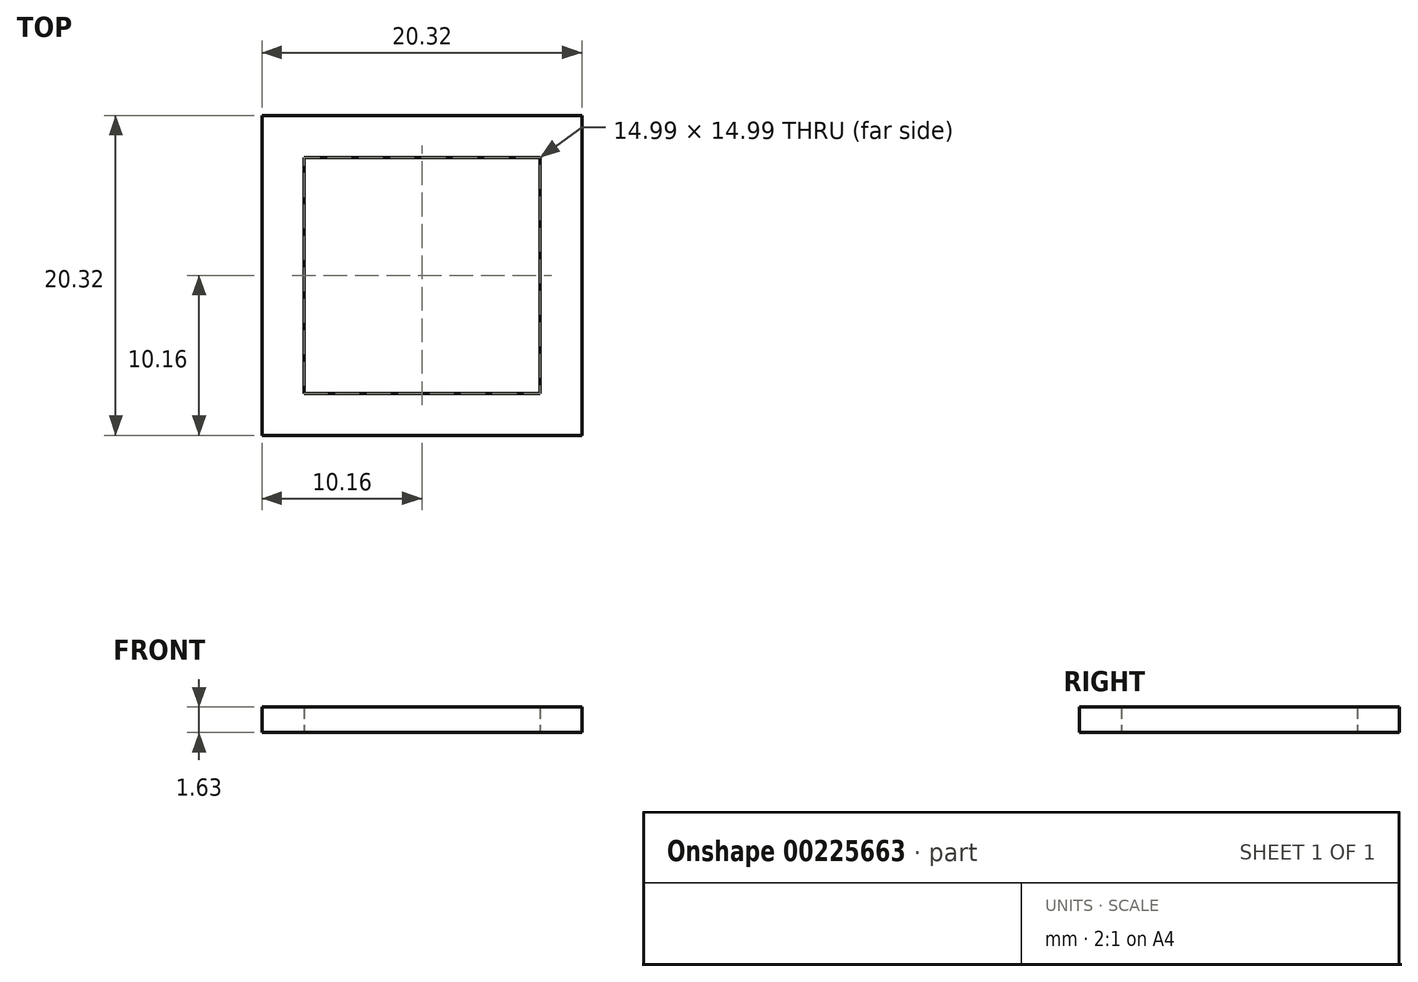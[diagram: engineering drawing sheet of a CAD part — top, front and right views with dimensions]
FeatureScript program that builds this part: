
annotation { "Feature Type Name" : "Feature", "Feature Type Description" : "" }
export const myFeature = defineFeature(function(context is Context, id is Id, definition is map)
    precondition{}
    {
        {
            var Q0;
            Q0=qCreatedBy(makeId("Top.planeOp"),FACE);
            var sketch = newSketch(context, id + "F0", { "sketchPlane" : qUnion([Q0])});
            skLineSegment(sketch, "E0.bottom", {"start": v(10.16, 10.16) * mm, "end": v(-10.16, 10.16) * mm});
            skLineSegment(sketch, "E0.top", {"start": v(10.16, -10.16) * mm, "end": v(-10.16, -10.16) * mm});
            skLineSegment(sketch, "E0.left", {"start": v(10.16, 10.16) * mm, "end": v(10.16, -10.16) * mm});
            skLineSegment(sketch, "E0.right", {"start": v(-10.16, 10.16) * mm, "end": v(-10.16, -10.16) * mm});
            skPoint(sketch, "E0.middle", {"position": v(0, 0) * mm});
            skLineSegment(sketch, "E1.bottom", {"start": v(7.5, 7.5) * mm, "end": v(-7.5, 7.5) * mm});
            skLineSegment(sketch, "E1.top", {"start": v(7.5, -7.5) * mm, "end": v(-7.5, -7.5) * mm});
            skLineSegment(sketch, "E1.left", {"start": v(7.5, 7.5) * mm, "end": v(7.5, -7.5) * mm});
            skLineSegment(sketch, "E1.right", {"start": v(-7.5, 7.5) * mm, "end": v(-7.5, -7.5) * mm});
            skSolve(sketch);
        }
        {
            var Q0;
            Q0 = qSketchRegion(id + "F0", true);
            extrude(context, id + "F1", {"entities" : qUnion([Q0]), "depth" : 1.63 * mm});
        }
    });
